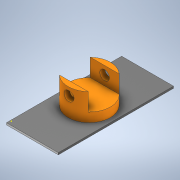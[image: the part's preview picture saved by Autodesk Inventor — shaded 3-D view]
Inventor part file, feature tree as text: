
AUTODESK INVENTOR PART (.ipt)
format: ipt  version: 2021 (Build 250183000, 183)  size: 146,944 bytes
history: native  units: mm
features: sketch x6, extrude x5
ambient origin geometry x8: Origin, YZ Plane, XZ Plane, XY Plane, X Axis, Y Axis, Z Axis, Center Point
bodies: Solid1 (feature_tree)
feature tree (11):
  extrude  "Extrusion1"  Depth=600.0mm
  sketch  "Sketch2"  dims[d2=10.0mm d3=0.0mm d4=220.0mm]
  extrude  "Extrusion2"  Depth=10.0mm
  extrude  "Extrusion3"  Depth=92.0mm TaperAngle=0.0deg
  extrude  "Extrusion4"  Depth=92.0mm TaperAngle=0.0deg
  extrude  "Extrusion5"  Depth=92.0mm TaperAngle=0.0deg
  sketch  "Sketch1"  dims[d0=270.0mm d1=600.0mm]
  sketch  "Sketch3"  dims[d5=140.0mm d6=0.0mm d7=92.0mm d8=0.0mm]
  sketch  "Sketch4"  dims[d9=50.0mm d10=92.0mm d11=0.0mm]
  sketch  "Sketch5"  dims[d12=50.0mm d13=92.0mm d14=0.0mm]
  sketch  "Sketch6"
